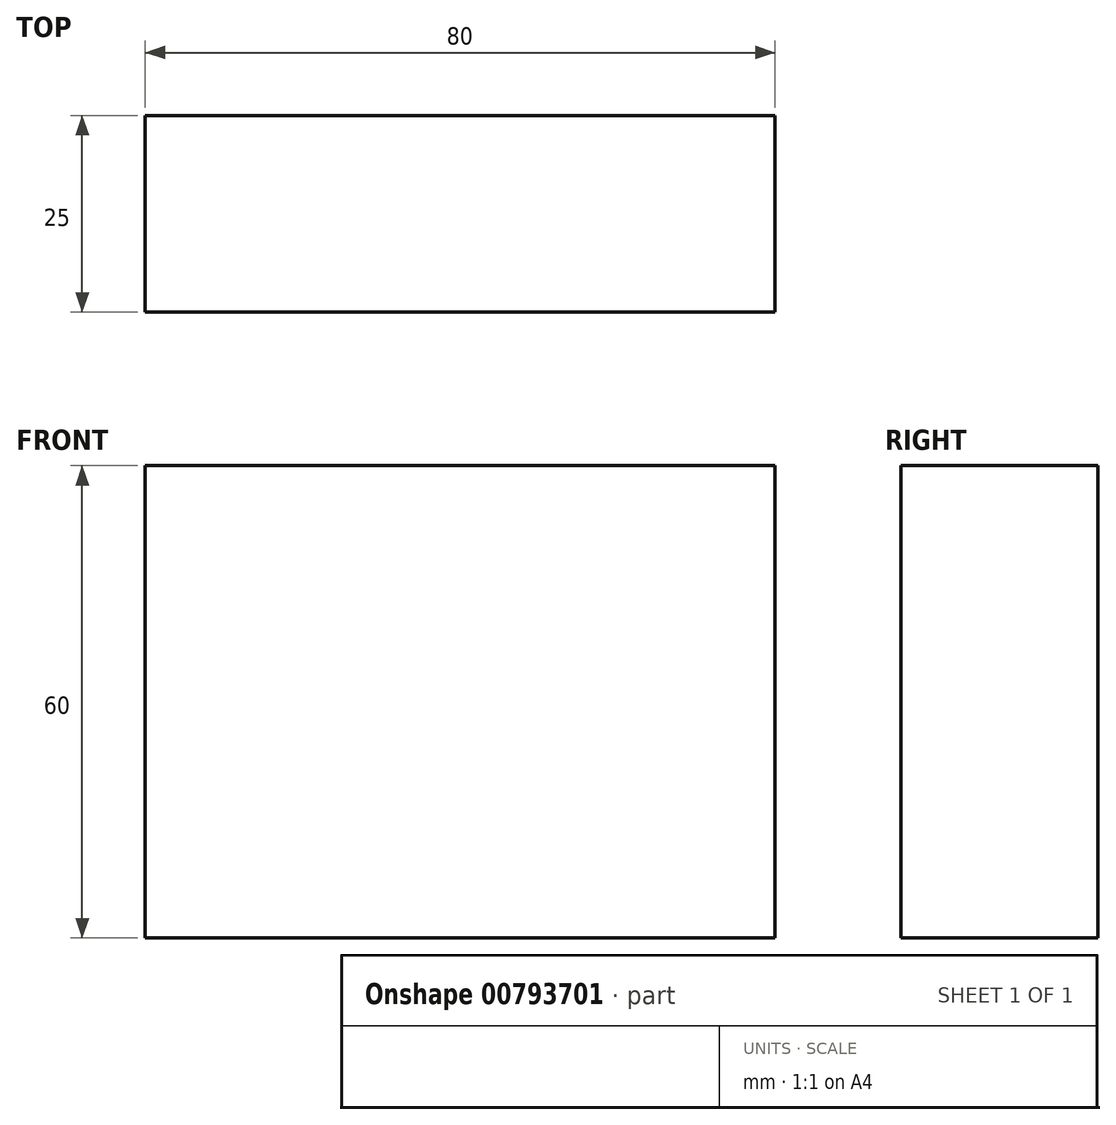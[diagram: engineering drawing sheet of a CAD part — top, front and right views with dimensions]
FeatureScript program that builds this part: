
annotation { "Feature Type Name" : "Feature", "Feature Type Description" : "" }
export const myFeature = defineFeature(function(context is Context, id is Id, definition is map)
    precondition{}
    {
        {
            var Q0;
            Q0=qCreatedBy(makeId("Front.planeOp"),FACE);
            var sketch = newSketch(context, id + "F0", { "sketchPlane" : qUnion([Q0])});
            skLineSegment(sketch, "E0.bottom", {"start": v(-40, 30) * mm, "end": v(40, 30) * mm});
            skLineSegment(sketch, "E0.top", {"start": v(-40, -30) * mm, "end": v(40, -30) * mm});
            skLineSegment(sketch, "E0.left", {"start": v(-40, 30) * mm, "end": v(-40, -30) * mm});
            skLineSegment(sketch, "E0.right", {"start": v(40, 30) * mm, "end": v(40, -30) * mm});
            skPoint(sketch, "E0.middle", {"position": v(0, 0) * mm});
            skLineSegment(sketch, "E1.bottom", {"start": v(57.7, 56.34) * mm, "end": v(77.7, 56.34) * mm});
            skLineSegment(sketch, "E1.top", {"start": v(57.7, 76.34) * mm, "end": v(77.7, 76.34) * mm});
            skLineSegment(sketch, "E1.left", {"start": v(57.7, 56.34) * mm, "end": v(57.7, 76.34) * mm});
            skLineSegment(sketch, "E1.right", {"start": v(77.7, 56.34) * mm, "end": v(77.7, 76.34) * mm});
            skPoint(sketch, "E1.middle", {"position": v(67.7, 66.34) * mm});
            skFitSpline(sketch, "E2", {"points": [v(0, 0) * mm, v(57.7, 66.34) * mm, v(77.7, 56.34) * mm], "startDerivative": vector(95.8, 142.89) * mm, "endDerivative": vector(55.11, -51.56) * mm});
            skFitSpline(sketch, "E3.0", {"points": [v(4.15, -2.78) * mm, v(8.14, 3.17) * mm, v(16.1, 15.05) * mm, v(25.81, 28.87) * mm, v(33.28, 38.71) * mm, v(38.69, 45.34) * mm, v(43.85, 51.05) * mm, v(47.89, 54.91) * mm, v(50.9, 57.38) * mm, v(53.03, 58.9) * mm, v(55, 60.08) * mm, v(56.78, 60.91) * mm, v(58.07, 61.32) * mm, v(58.97, 61.5) * mm, v(59.83, 61.6) * mm, v(60.85, 61.6) * mm, v(62.08, 61.39) * mm, v(63.38, 60.98) * mm, v(65.21, 60.14) * mm, v(67.7, 58.52) * mm, v(70.9, 55.85) * mm, v(73.13, 53.77) * mm, v(74.28, 52.7) * mm]});
            skSolve(sketch);
        }
        {
            var Q0;
            Q0=makeQuery(id+"F0.imprint","IMPRINT",FACE,{"disambiguationData":[TD([[makeQuery(id+"F0.imprint","IMPRINT",EDGE,{"derivedFrom":sQuery(id+"F0.wireOp",EDGE,"E0.top")}),1.0]])]});
            extrude(context, id + "F1", {"entities" : qUnion([Q0]), "depth" : 25 * mm, "offsetDistance" : 25 * mm});
        }
    });
